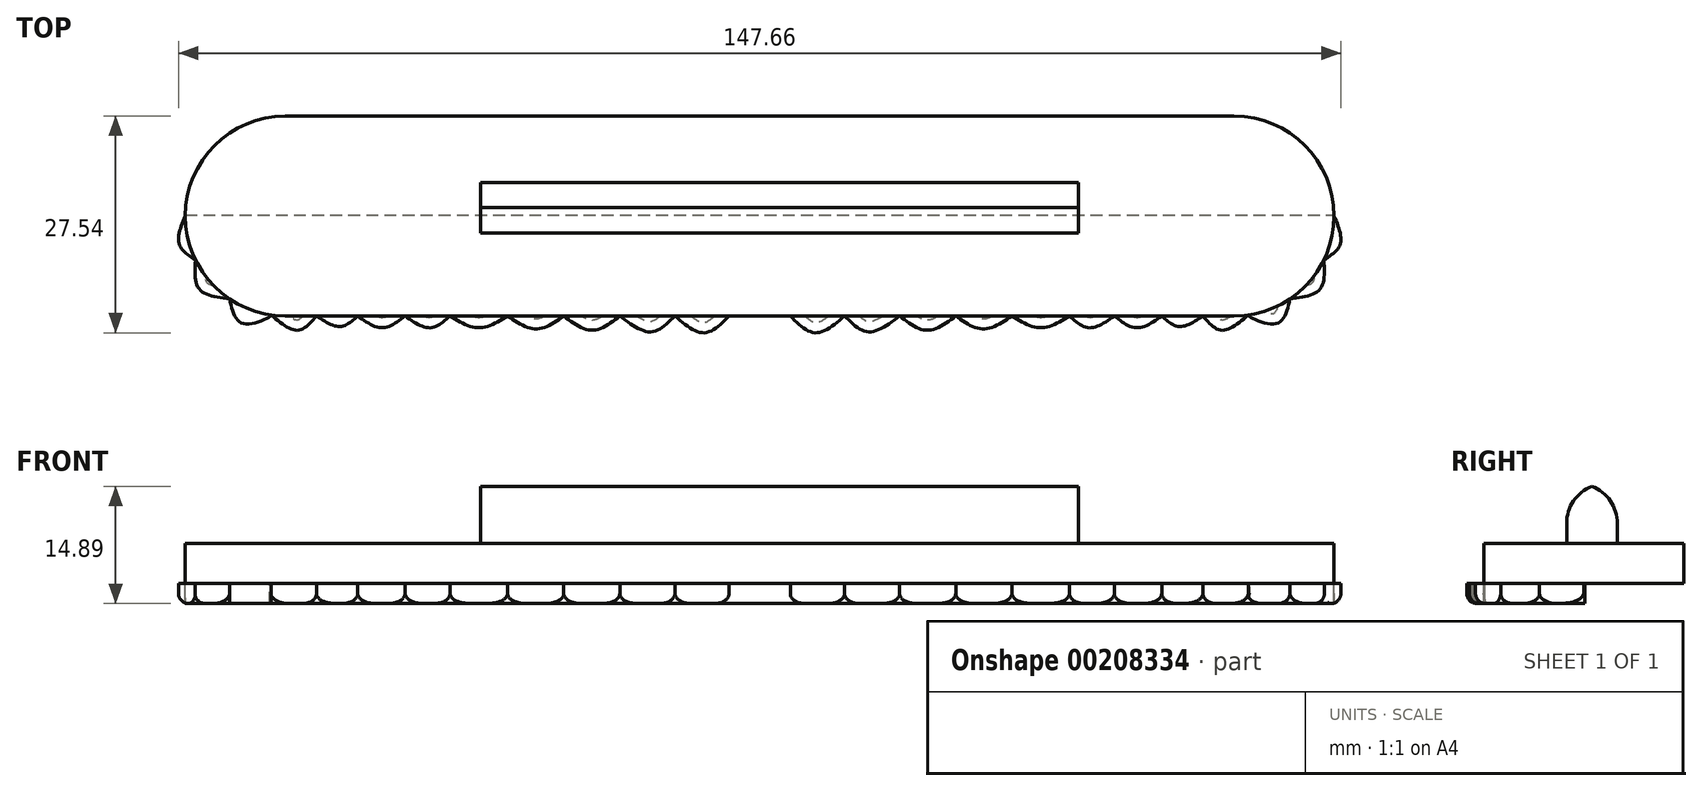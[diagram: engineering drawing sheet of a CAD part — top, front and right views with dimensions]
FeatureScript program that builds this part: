
annotation { "Feature Type Name" : "Feature", "Feature Type Description" : "" }
export const myFeature = defineFeature(function(context is Context, id is Id, definition is map)
    precondition{}
    {
        {
            var Q0;
            Q0=qCreatedBy(makeId("Top.planeOp"),FACE);
            var sketch = newSketch(context, id + "F0", { "sketchPlane" : qUnion([Q0])});
            skLineSegment(sketch, "E0.bottom", {"start": v(-28.22, 12.55) * mm, "end": v(92.3, 12.55) * mm});
            skLineSegment(sketch, "E0.top", {"start": v(-28.22, -12.85) * mm, "end": v(92.3, -12.85) * mm});
            skLineSegment(sketch, "E0.left", {"start": v(-28.22, 12.55) * mm, "end": v(-28.22, -12.85) * mm});
            skLineSegment(sketch, "E0.right", {"start": v(92.3, 12.55) * mm, "end": v(92.3, -12.85) * mm});
            skArc(sketch, "E1", {"start": v(-28.22, 12.55) * mm, "mid": v(-40.92, -0.15) * mm, "end": v(-28.22, -12.85) * mm});
            skArc(sketch, "E2", {"start": v(92.3, -12.85) * mm, "mid": v(105, -0.15) * mm, "end": v(92.3, 12.55) * mm});
            skSolve(sketch);
        }
        {
            var Q0;
            Q0=makeQuery(id+"F0.imprint","IMPRINT",FACE,{"disambiguationData":[TD([[makeQuery(id+"F0.imprint","IMPRINT",EDGE,{"derivedFrom":sQuery(id+"F0.wireOp",EDGE,"E0.left")}),-1.0]])]});
            var Q1;
            Q1=makeQuery(id+"F0.imprint","IMPRINT",FACE,{"disambiguationData":[TD([[makeQuery(id+"F0.imprint","IMPRINT",EDGE,{"derivedFrom":sQuery(id+"F0.wireOp",EDGE,"E0.bottom")}),-1.0]])]});
            var Q2;
            Q2=makeQuery(id+"F0.imprint","IMPRINT",FACE,{"disambiguationData":[TD([[makeQuery(id+"F0.imprint","IMPRINT",EDGE,{"derivedFrom":sQuery(id+"F0.wireOp",EDGE,"E0.right")}),1.0]])]});
            extrude(context, id + "F1", {"entities" : qUnion([Q0, Q1, Q2]), "depth" : 5.08 * mm});
        }
        {
            var Q0;
            Q0=makeQuery(id+"F1.opExtrude","CAP_FACE",FACE,{"disambiguationData":[OSD([sQuery(id+"F0.wireOp",EDGE,"E0.bottom"),sQuery(id+"F0.wireOp",EDGE,"E0.top"),sQuery(id+"F0.wireOp",EDGE,"E1"),sQuery(id+"F0.wireOp",EDGE,"E2")])],"isStart":true});
            var sketch = newSketch(context, id + "F2", { "sketchPlane" : qUnion([Q0])});
            skFitSpline(sketch, "E3", {"points": [v(-35.3, 10.7) * mm, v(-33.3, 13.87) * mm, v(-30.02, 12.73) * mm, v(-30.24, 12.7) * mm, v(-30.21, 12.7) * mm], "startDerivative": vector(2.37, 10.41) * mm, "endDerivative": vector(1.4, 0.2) * mm});
            skFitSpline(sketch, "E4", {"points": [v(-30.02, 12.73) * mm, v(-26.65, 14.67) * mm, v(-24.27, 12.85) * mm], "startDerivative": vector(6.67, 5.65) * mm, "endDerivative": vector(4.8, -5.64) * mm});
            skFitSpline(sketch, "E5", {"points": [v(-24.27, 12.85) * mm, v(-21.25, 14.2) * mm, v(-19.03, 12.85) * mm], "startDerivative": vector(5.94, 3.95) * mm, "endDerivative": vector(4.5, -4.1) * mm});
            skFitSpline(sketch, "E6", {"points": [v(-19.03, 12.85) * mm, v(-15.86, 14.35) * mm, v(-13, 12.85) * mm], "startDerivative": vector(6.31, 4.46) * mm, "endDerivative": vector(5.74, -4.52) * mm});
            skFitSpline(sketch, "E7", {"points": [v(-13, 12.85) * mm, v(-9.83, 14.35) * mm, v(-7.3, 12.85) * mm], "startDerivative": vector(6.28, 4.43) * mm, "endDerivative": vector(5.12, -4.56) * mm});
            skFitSpline(sketch, "E8", {"points": [v(-7.3, 12.85) * mm, v(-3.65, 14.35) * mm, v(0, 12.85) * mm], "startDerivative": vector(7.3, 4.49) * mm, "endDerivative": vector(7.3, -4.49) * mm});
            skFitSpline(sketch, "E9", {"points": [v(0, 12.85) * mm, v(3.65, 14.5) * mm, v(7.14, 12.85) * mm], "startDerivative": vector(7.28, 4.95) * mm, "endDerivative": vector(7, -4.98) * mm});
            skFitSpline(sketch, "E10", {"points": [v(7.14, 12.85) * mm, v(10.79, 14.67) * mm, v(14.27, 12.85) * mm], "startDerivative": vector(7.28, 5.42) * mm, "endDerivative": vector(7, -5.46) * mm});
            skLineSegment(sketch, "E11", {"start": v(32.04, 13.5) * mm, "end": v(32.04, 65.15) * mm});
            skPoint(sketch, "E11.startSnap0", {"position": v(32.04, 12.85) * mm});
            skLineSegment(sketch, "E12", {"start": v(32.04, 65.15) * mm, "end": v(32.04, -46.58) * mm});
            skPoint(sketch, "E12.endSnap0", {"position": v(32.04, -12.55) * mm});
            skLineSegment(sketch, "E13", {"start": v(-54.93, 0.15) * mm, "end": v(124.28, 0) * mm});
            skPoint(sketch, "E13.startSnap0", {"position": v(-40.92, 0.15) * mm});
            skFitSpline(sketch, "E14", {"points": [v(14.27, 12.85) * mm, v(18.2, 14.86) * mm, v(21.27, 12.85) * mm], "startDerivative": vector(7.77, 5.95) * mm, "endDerivative": vector(6.2, -6.13) * mm});
            skFitSpline(sketch, "E15", {"points": [v(21.27, 12.85) * mm, v(24.96, 14.99) * mm, v(28.15, 12.85) * mm], "startDerivative": vector(7.36, 6.35) * mm, "endDerivative": vector(6.41, -6.46) * mm});
            skFitSpline(sketch, "E16", {"points": [v(28.15, 12.85) * mm, v(32.04, 14.99) * mm, v(35.66, 12.85) * mm], "startDerivative": vector(7.75, 6.37) * mm, "endDerivative": vector(7.25, -6.43) * mm});
            skFitSpline(sketch, "E17", {"points": [v(-35.3, 10.7) * mm, v(-39.13, 9.45) * mm, v(-39.62, 5.76) * mm], "startDerivative": vector(-9.17, -1.14) * mm, "endDerivative": vector(0.62, -8.8) * mm});
            skFitSpline(sketch, "E18", {"points": [v(-39.62, 5.76) * mm, v(-41.72, 3.67) * mm, v(-40.92, 0.15) * mm], "startDerivative": vector(-5.81, -3.84) * mm, "endDerivative": vector(3.06, -7.3) * mm});
            skFitSpline(sketch, "E19.MirrorCS", {"points": [v(49.8, 12.85) * mm, v(45.89, 14.86) * mm, v(42.81, 12.85) * mm], "startDerivative": vector(-7.77, 5.95) * mm, "endDerivative": vector(-6.2, -6.13) * mm});
            skFitSpline(sketch, "E20.MirrorCS", {"points": [v(42.81, 12.85) * mm, v(39.12, 14.99) * mm, v(35.92, 12.85) * mm], "startDerivative": vector(-7.36, 6.35) * mm, "endDerivative": vector(-6.41, -6.46) * mm});
            skFitSpline(sketch, "E21.MirrorCS", {"points": [v(56.94, 12.85) * mm, v(53.3, 14.67) * mm, v(49.8, 12.85) * mm], "startDerivative": vector(-7.28, 5.42) * mm, "endDerivative": vector(-7, -5.46) * mm});
            skFitSpline(sketch, "E22.MirrorCS", {"points": [v(64.08, 12.85) * mm, v(60.43, 14.5) * mm, v(56.94, 12.85) * mm], "startDerivative": vector(-7.28, 4.95) * mm, "endDerivative": vector(-7, -4.98) * mm});
            skFitSpline(sketch, "E23.MirrorCS", {"points": [v(71.38, 12.85) * mm, v(67.73, 14.35) * mm, v(64.08, 12.85) * mm], "startDerivative": vector(-7.3, 4.49) * mm, "endDerivative": vector(-7.3, -4.49) * mm});
            skFitSpline(sketch, "E24.MirrorCS", {"points": [v(77.09, 12.85) * mm, v(73.91, 14.35) * mm, v(71.38, 12.85) * mm], "startDerivative": vector(-6.28, 4.43) * mm, "endDerivative": vector(-5.12, -4.56) * mm});
            skFitSpline(sketch, "E25.MirrorCS", {"points": [v(83.11, 12.85) * mm, v(79.94, 14.35) * mm, v(77.09, 12.85) * mm], "startDerivative": vector(-6.31, 4.46) * mm, "endDerivative": vector(-5.74, -4.52) * mm});
            skFitSpline(sketch, "E26.MirrorCS", {"points": [v(88.35, 12.85) * mm, v(85.33, 14.2) * mm, v(83.11, 12.85) * mm], "startDerivative": vector(-5.94, 3.95) * mm, "endDerivative": vector(-4.5, -4.1) * mm});
            skFitSpline(sketch, "E27.MirrorCS", {"points": [v(94.1, 12.73) * mm, v(90.73, 14.67) * mm, v(88.35, 12.85) * mm], "startDerivative": vector(-6.67, 5.65) * mm, "endDerivative": vector(-4.8, -5.64) * mm});
            skFitSpline(sketch, "E28.MirrorCS", {"points": [v(99.39, 10.7) * mm, v(97.39, 13.87) * mm, v(94.1, 12.73) * mm, v(94.32, 12.7) * mm, v(94.29, 12.7) * mm], "startDerivative": vector(-2.37, 10.41) * mm, "endDerivative": vector(-1.4, 0.2) * mm});
            skFitSpline(sketch, "E29.MirrorCS", {"points": [v(99.39, 10.7) * mm, v(103.21, 9.45) * mm, v(103.7, 5.76) * mm], "startDerivative": vector(9.17, -1.14) * mm, "endDerivative": vector(-0.62, -8.8) * mm});
            skFitSpline(sketch, "E30.MirrorCS", {"points": [v(103.7, 5.76) * mm, v(105.8, 3.67) * mm, v(105, 0.15) * mm], "startDerivative": vector(5.81, -3.84) * mm, "endDerivative": vector(-3.06, -7.3) * mm});
            skFitSpline(sketch, "E31.MirrorCS", {"points": [v(-39.63, -5.47) * mm, v(-41.72, -3.38) * mm, v(-40.92, 0.13) * mm], "startDerivative": vector(-5.8, 3.85) * mm, "endDerivative": vector(3.08, 7.3) * mm});
            skFitSpline(sketch, "E32.MirrorCS", {"points": [v(-35.33, -10.42) * mm, v(-39.15, -9.17) * mm, v(-39.63, -5.47) * mm], "startDerivative": vector(-9.17, 1.15) * mm, "endDerivative": vector(0.64, 8.8) * mm});
            skFitSpline(sketch, "E33.MirrorCS", {"points": [v(-35.33, -10.42) * mm, v(-33.33, -13.6) * mm, v(-30.05, -12.46) * mm, v(-30.27, -12.43) * mm, v(-30.23, -12.43) * mm], "startDerivative": vector(2.36, -10.41) * mm, "endDerivative": vector(1.4, -0.2) * mm});
            skFitSpline(sketch, "E34.MirrorCS", {"points": [v(-30.05, -12.46) * mm, v(-26.67, -14.4) * mm, v(-24.29, -12.6) * mm], "startDerivative": vector(6.66, -5.66) * mm, "endDerivative": vector(4.81, 5.63) * mm});
            skFitSpline(sketch, "E35.MirrorCS", {"points": [v(-24.29, -12.6) * mm, v(-21.28, -13.94) * mm, v(-19.06, -12.6) * mm], "startDerivative": vector(5.93, -3.96) * mm, "endDerivative": vector(4.5, 4.1) * mm});
            skFitSpline(sketch, "E36.MirrorCS", {"points": [v(-19.06, -12.6) * mm, v(-15.89, -14.1) * mm, v(-13.03, -12.62) * mm], "startDerivative": vector(6.3, -4.47) * mm, "endDerivative": vector(5.75, 4.51) * mm});
            skFitSpline(sketch, "E37.MirrorCS", {"points": [v(-13.03, -12.62) * mm, v(-9.86, -14.12) * mm, v(-7.32, -12.63) * mm], "startDerivative": vector(6.27, -4.44) * mm, "endDerivative": vector(5.13, 4.55) * mm});
            skFitSpline(sketch, "E38.MirrorCS", {"points": [v(-7.32, -12.63) * mm, v(-3.67, -14.13) * mm, v(-0.02, -12.64) * mm], "startDerivative": vector(7.29, -4.5) * mm, "endDerivative": vector(7.3, 4.47) * mm});
            skFitSpline(sketch, "E39.MirrorCS", {"points": [v(-0.02, -12.64) * mm, v(3.62, -14.3) * mm, v(7.12, -12.65) * mm], "startDerivative": vector(7.27, -4.96) * mm, "endDerivative": vector(7, 4.97) * mm});
            skFitSpline(sketch, "E40.MirrorCS", {"points": [v(7.12, -12.65) * mm, v(10.76, -14.47) * mm, v(14.25, -12.66) * mm], "startDerivative": vector(7.27, -5.44) * mm, "endDerivative": vector(7, 5.44) * mm});
            skFitSpline(sketch, "E41.MirrorCS", {"points": [v(14.25, -12.66) * mm, v(18.16, -14.68) * mm, v(21.24, -12.68) * mm], "startDerivative": vector(7.76, -5.96) * mm, "endDerivative": vector(6.2, 6.12) * mm});
            skFitSpline(sketch, "E42.MirrorCS", {"points": [v(14.25, -12.66) * mm, v(18.16, -14.68) * mm, v(21.24, -12.68) * mm], "startDerivative": vector(7.76, -5.96) * mm, "endDerivative": vector(6.2, 6.12) * mm});
            skFitSpline(sketch, "E43.MirrorCS", {"points": [v(21.24, -12.68) * mm, v(24.93, -14.82) * mm, v(28.13, -12.69) * mm], "startDerivative": vector(7.35, -6.36) * mm, "endDerivative": vector(6.42, 6.45) * mm});
            skFitSpline(sketch, "E44.MirrorCS", {"points": [v(28.13, -12.69) * mm, v(32.01, -14.83) * mm, v(35.64, -12.7) * mm], "startDerivative": vector(7.74, -6.38) * mm, "endDerivative": vector(7.26, 6.42) * mm});
            skFitSpline(sketch, "E45.MirrorCS", {"points": [v(42.8, -12.71) * mm, v(39.1, -14.84) * mm, v(35.9, -12.7) * mm], "startDerivative": vector(-7.37, -6.34) * mm, "endDerivative": vector(-6.4, 6.47) * mm});
            skFitSpline(sketch, "E46.MirrorCS", {"points": [v(49.78, -12.73) * mm, v(45.86, -14.73) * mm, v(42.8, -12.71) * mm], "startDerivative": vector(-7.78, -5.94) * mm, "endDerivative": vector(-6.18, 6.14) * mm});
            skFitSpline(sketch, "E47.MirrorCS", {"points": [v(56.92, -12.74) * mm, v(53.27, -14.55) * mm, v(49.78, -12.73) * mm], "startDerivative": vector(-7.29, -5.41) * mm, "endDerivative": vector(-6.98, 5.47) * mm});
            skFitSpline(sketch, "E48.MirrorCS", {"points": [v(64.06, -12.75) * mm, v(60.4, -14.4) * mm, v(56.92, -12.74) * mm], "startDerivative": vector(-7.29, -4.94) * mm, "endDerivative": vector(-6.99, 5) * mm});
            skFitSpline(sketch, "E49.MirrorCS", {"points": [v(77.06, -12.77) * mm, v(73.89, -14.26) * mm, v(71.35, -12.76) * mm], "startDerivative": vector(-6.29, -4.42) * mm, "endDerivative": vector(-5.11, 4.57) * mm});
            skFitSpline(sketch, "E50.MirrorCS", {"points": [v(77.06, -12.77) * mm, v(73.89, -14.26) * mm, v(71.35, -12.76) * mm], "startDerivative": vector(-6.29, -4.42) * mm, "endDerivative": vector(-5.11, 4.57) * mm});
            skFitSpline(sketch, "E51.MirrorCS", {"points": [v(77.06, -12.77) * mm, v(73.89, -14.26) * mm, v(71.35, -12.76) * mm], "startDerivative": vector(-6.29, -4.42) * mm, "endDerivative": vector(-5.11, 4.57) * mm});
            skFitSpline(sketch, "E52.MirrorCS", {"points": [v(71.35, -12.76) * mm, v(67.7, -14.25) * mm, v(64.06, -12.75) * mm], "startDerivative": vector(-7.3, -4.47) * mm, "endDerivative": vector(-7.29, 4.5) * mm});
            skFitSpline(sketch, "E53.MirrorCS", {"points": [v(83.1, -12.78) * mm, v(79.92, -14.27) * mm, v(77.06, -12.77) * mm], "startDerivative": vector(-6.32, -4.45) * mm, "endDerivative": vector(-5.73, 4.53) * mm});
            skFitSpline(sketch, "E54.MirrorCS", {"points": [v(88.32, -12.8) * mm, v(85.3, -14.12) * mm, v(83.1, -12.78) * mm], "startDerivative": vector(-5.95, -3.94) * mm, "endDerivative": vector(-4.5, 4.11) * mm});
            skFitSpline(sketch, "E55.MirrorCS", {"points": [v(94.08, -12.67) * mm, v(90.7, -14.6) * mm, v(88.32, -12.8) * mm], "startDerivative": vector(-6.68, -5.64) * mm, "endDerivative": vector(-4.8, 5.65) * mm});
            skFitSpline(sketch, "E56.MirrorCS", {"points": [v(99.37, -10.65) * mm, v(97.36, -13.83) * mm, v(94.08, -12.67) * mm, v(94.3, -12.64) * mm, v(94.27, -12.65) * mm], "startDerivative": vector(-2.4, -10.4) * mm, "endDerivative": vector(-1.4, -0.2) * mm});
            skFitSpline(sketch, "E57.MirrorCS", {"points": [v(103.69, -5.72) * mm, v(105.79, -3.64) * mm, v(105, -0.12) * mm], "startDerivative": vector(5.82, 3.83) * mm, "endDerivative": vector(-3.05, 7.31) * mm});
            skFitSpline(sketch, "E58.MirrorCS", {"points": [v(99.37, -10.65) * mm, v(103.2, -9.42) * mm, v(103.69, -5.72) * mm], "startDerivative": vector(9.17, 1.12) * mm, "endDerivative": vector(-0.6, 8.8) * mm});
            skSolve(sketch);
        }
        {
            var Q0;
            {var subQ0=sQuery(id+"F2.wireOp",EDGE,"E7");Q0=makeQuery(id+"F2.imprint","IMPRINT",FACE,{"disambiguationData":[TD([[makeQuery(id+"F2.imprint","IMPRINT",EDGE,{"derivedFrom":subQ0}),-1.0]])]});}
            var Q1;
            {var subQ0=sQuery(id+"F2.wireOp",EDGE,"E8");Q1=makeQuery(id+"F2.imprint","IMPRINT",FACE,{"disambiguationData":[TD([[makeQuery(id+"F2.imprint","IMPRINT",EDGE,{"derivedFrom":subQ0}),-1.0]])]});}
            var Q2;
            {var subQ0=sQuery(id+"F2.wireOp",EDGE,"E6");Q2=makeQuery(id+"F2.imprint","IMPRINT",FACE,{"disambiguationData":[TD([[makeQuery(id+"F2.imprint","IMPRINT",EDGE,{"derivedFrom":subQ0}),-1.0]])]});}
            var Q3;
            {var subQ0=sQuery(id+"F2.wireOp",EDGE,"E5");Q3=makeQuery(id+"F2.imprint","IMPRINT",FACE,{"disambiguationData":[TD([[makeQuery(id+"F2.imprint","IMPRINT",EDGE,{"derivedFrom":subQ0}),-1.0]])]});}
            var Q4;
            {var subQ0=sQuery(id+"F2.wireOp",EDGE,"E4");Q4=makeQuery(id+"F2.imprint","IMPRINT",FACE,{"disambiguationData":[TD([[makeQuery(id+"F2.imprint","IMPRINT",EDGE,{"derivedFrom":subQ0}),-1.0]])]});}
            var Q5;
            {var subQ0=sQuery(id+"F2.wireOp",EDGE,"E9");Q5=makeQuery(id+"F2.imprint","IMPRINT",FACE,{"disambiguationData":[TD([[makeQuery(id+"F2.imprint","IMPRINT",EDGE,{"derivedFrom":subQ0}),-1.0]])]});}
            var Q6;
            {var subQ0=sQuery(id+"F2.wireOp",EDGE,"E10");Q6=makeQuery(id+"F2.imprint","IMPRINT",FACE,{"disambiguationData":[TD([[makeQuery(id+"F2.imprint","IMPRINT",EDGE,{"derivedFrom":subQ0}),-1.0]])]});}
            var Q7;
            {var subQ0=sQuery(id+"F2.wireOp",EDGE,"E14");Q7=makeQuery(id+"F2.imprint","IMPRINT",FACE,{"disambiguationData":[TD([[makeQuery(id+"F2.imprint","IMPRINT",EDGE,{"derivedFrom":subQ0}),-1.0]])]});}
            var Q8;
            {var subQ0=sQuery(id+"F2.wireOp",EDGE,"E15");Q8=makeQuery(id+"F2.imprint","IMPRINT",FACE,{"disambiguationData":[TD([[makeQuery(id+"F2.imprint","IMPRINT",EDGE,{"derivedFrom":subQ0}),-1.0]])]});}
            var Q9;
            {var subQ0=sQuery(id+"F2.wireOp",EDGE,"E12");var subQ1=makeQuery(id+"F2.imprint","IMPRINT",VERTEX,{"derivedFrom":subQ0});Q9=makeQuery(id+"F2.imprint","IMPRINT",FACE,{"disambiguationData":[TD([[makeQuery(id+"F2.imprint","IMPRINT",EDGE,{"disambiguationData":[TD([[subQ1,1.0]])],"derivedFrom":subQ0}),-1.0]])]});}
            var Q10;
            {var subQ0=sQuery(id+"F2.wireOp",EDGE,"E12");var subQ1=makeQuery(id+"F2.imprint","IMPRINT",VERTEX,{"derivedFrom":subQ0});Q10=makeQuery(id+"F2.imprint","IMPRINT",FACE,{"disambiguationData":[TD([[makeQuery(id+"F2.imprint","IMPRINT",EDGE,{"disambiguationData":[TD([[subQ1,1.0]])],"derivedFrom":subQ0}),1.0]])]});}
            var Q11;
            {var subQ0=sQuery(id+"F2.wireOp",EDGE,"E20.MirrorCS");Q11=makeQuery(id+"F2.imprint","IMPRINT",FACE,{"disambiguationData":[TD([[makeQuery(id+"F2.imprint","IMPRINT",EDGE,{"derivedFrom":subQ0}),1.0]])]});}
            var Q12;
            {var subQ0=sQuery(id+"F2.wireOp",EDGE,"E19.MirrorCS");Q12=makeQuery(id+"F2.imprint","IMPRINT",FACE,{"disambiguationData":[TD([[makeQuery(id+"F2.imprint","IMPRINT",EDGE,{"derivedFrom":subQ0}),1.0]])]});}
            var Q13;
            {var subQ0=sQuery(id+"F2.wireOp",EDGE,"E21.MirrorCS");Q13=makeQuery(id+"F2.imprint","IMPRINT",FACE,{"disambiguationData":[TD([[makeQuery(id+"F2.imprint","IMPRINT",EDGE,{"derivedFrom":subQ0}),1.0]])]});}
            var Q14;
            {var subQ0=sQuery(id+"F2.wireOp",EDGE,"E22.MirrorCS");Q14=makeQuery(id+"F2.imprint","IMPRINT",FACE,{"disambiguationData":[TD([[makeQuery(id+"F2.imprint","IMPRINT",EDGE,{"derivedFrom":subQ0}),1.0]])]});}
            var Q15;
            {var subQ0=sQuery(id+"F2.wireOp",EDGE,"E23.MirrorCS");Q15=makeQuery(id+"F2.imprint","IMPRINT",FACE,{"disambiguationData":[TD([[makeQuery(id+"F2.imprint","IMPRINT",EDGE,{"derivedFrom":subQ0}),1.0]])]});}
            var Q16;
            {var subQ0=sQuery(id+"F2.wireOp",EDGE,"E24.MirrorCS");Q16=makeQuery(id+"F2.imprint","IMPRINT",FACE,{"disambiguationData":[TD([[makeQuery(id+"F2.imprint","IMPRINT",EDGE,{"derivedFrom":subQ0}),1.0]])]});}
            var Q17;
            {var subQ0=sQuery(id+"F2.wireOp",EDGE,"E25.MirrorCS");Q17=makeQuery(id+"F2.imprint","IMPRINT",FACE,{"disambiguationData":[TD([[makeQuery(id+"F2.imprint","IMPRINT",EDGE,{"derivedFrom":subQ0}),1.0]])]});}
            var Q18;
            {var subQ0=sQuery(id+"F2.wireOp",EDGE,"E26.MirrorCS");Q18=makeQuery(id+"F2.imprint","IMPRINT",FACE,{"disambiguationData":[TD([[makeQuery(id+"F2.imprint","IMPRINT",EDGE,{"derivedFrom":subQ0}),1.0]])]});}
            var Q19;
            {var subQ0=sQuery(id+"F2.wireOp",EDGE,"E27.MirrorCS");Q19=makeQuery(id+"F2.imprint","IMPRINT",FACE,{"disambiguationData":[TD([[makeQuery(id+"F2.imprint","IMPRINT",EDGE,{"derivedFrom":subQ0}),1.0]])]});}
            var Q20;
            {var subQ0=sQuery(id+"F2.wireOp",EDGE,"E28.MirrorCS");var subQ1=makeQuery(id+"F1.opExtrude","CAP_EDGE",EDGE,{"disambiguationData":[OSD([sQuery(id+"F0.wireOp",EDGE,"E2")])],"isStart":true});var subQ4=makeQuery(id+"F2.imprint","INTERSECT",VERTEX,{"disambiguationData":[OD(0.0)],"derivedFrom":[subQ1,subQ0]});Q20=makeQuery(id+"F2.imprint","IMPRINT",FACE,{"disambiguationData":[TD([[makeQuery(id+"F2.imprint","IMPRINT",EDGE,{"disambiguationData":[TD([[subQ4,1.0]])],"derivedFrom":subQ0}),-1.0]])]});}
            var Q21;
            {var subQ0=sQuery(id+"F2.wireOp",EDGE,"E29.MirrorCS");Q21=makeQuery(id+"F2.imprint","IMPRINT",FACE,{"disambiguationData":[TD([[makeQuery(id+"F2.imprint","IMPRINT",EDGE,{"derivedFrom":subQ0}),-1.0]])]});}
            var Q22;
            {var subQ0=sQuery(id+"F2.wireOp",EDGE,"E30.MirrorCS");Q22=makeQuery(id+"F2.imprint","IMPRINT",FACE,{"disambiguationData":[TD([[makeQuery(id+"F2.imprint","IMPRINT",EDGE,{"derivedFrom":subQ0}),-1.0]])]});}
            var Q23;
            {var subQ0=sQuery(id+"F2.wireOp",EDGE,"E17");Q23=makeQuery(id+"F2.imprint","IMPRINT",FACE,{"disambiguationData":[TD([[makeQuery(id+"F2.imprint","IMPRINT",EDGE,{"derivedFrom":subQ0}),1.0]])]});}
            var Q24;
            {var subQ0=sQuery(id+"F2.wireOp",EDGE,"E18");Q24=makeQuery(id+"F2.imprint","IMPRINT",FACE,{"disambiguationData":[TD([[makeQuery(id+"F2.imprint","IMPRINT",EDGE,{"derivedFrom":subQ0}),1.0]])]});}
            var Q25;
            {var subQ0=sQuery(id+"F2.wireOp",EDGE,"E3");var subQ1=makeQuery(id+"F1.opExtrude","CAP_EDGE",EDGE,{"disambiguationData":[OSD([sQuery(id+"F0.wireOp",EDGE,"E1")])],"isStart":true});var subQ4=makeQuery(id+"F2.imprint","INTERSECT",VERTEX,{"disambiguationData":[OD(0.0)],"derivedFrom":[subQ1,subQ0]});Q25=makeQuery(id+"F2.imprint","IMPRINT",FACE,{"disambiguationData":[TD([[makeQuery(id+"F2.imprint","IMPRINT",EDGE,{"disambiguationData":[TD([[subQ4,1.0]])],"derivedFrom":subQ0}),1.0]])]});}
            extrude(context, id + "F3", {"entities" : qUnion([Q0, Q1, Q2, Q3, Q4, Q5, Q6, Q7, Q8, Q9, Q10, Q11, Q12, Q13, Q14, Q15, Q16, Q17, Q18, Q19, Q20, Q21, Q22, Q23, Q24, Q25]), "depth" : 2.54 * mm});
        }
        {
            var Q0;
            Q0=makeQuery(id+"F1.opExtrude","CAP_FACE",FACE,{"disambiguationData":[OSD([sQuery(id+"F0.wireOp",EDGE,"E0.bottom"),sQuery(id+"F0.wireOp",EDGE,"E0.top"),sQuery(id+"F0.wireOp",EDGE,"E1"),sQuery(id+"F0.wireOp",EDGE,"E2")])],"isStart":true});
            var sketch = newSketch(context, id + "F4", { "sketchPlane" : qUnion([Q0])});
            skLineSegment(sketch, "E59", {"start": v(-40.92, 0) * mm, "end": v(105, 0) * mm});
            skLineSegment(sketch, "E60", {"start": v(-28.22, 12.85) * mm, "end": v(92.3, 12.85) * mm});
            skArc(sketch, "E61", {"start": v(-28.22, 12.85) * mm, "mid": v(-37.26, 9.08) * mm, "end": v(-40.92, 0) * mm});
            skArc(sketch, "E62", {"start": v(105, 0) * mm, "mid": v(101.34, 9.08) * mm, "end": v(92.3, 12.85) * mm});
            skSolve(sketch);
        }
        {
            var Q0;
            Q0=makeQuery(id+"F4.imprint","IMPRINT",FACE,{"disambiguationData":[TD([[makeQuery(id+"F4.imprint","IMPRINT",EDGE,{"derivedFrom":sQuery(id+"F4.wireOp",EDGE,"E59")}),1.0]])]});
            extrude(context, id + "F5", {"entities" : qUnion([Q0]), "depth" : 2.54 * mm});
        }
        {
            var Q0;
            Q0=makeQuery(id+"F1.opExtrude","CAP_FACE",FACE,{"disambiguationData":[OSD([sQuery(id+"F0.wireOp",EDGE,"E0.bottom"),sQuery(id+"F0.wireOp",EDGE,"E0.top"),sQuery(id+"F0.wireOp",EDGE,"E1"),sQuery(id+"F0.wireOp",EDGE,"E2")])],"isStart":false});
            var sketch = newSketch(context, id + "F6", { "sketchPlane" : qUnion([Q0])});
            skLineSegment(sketch, "E63.bottom", {"start": v(-3.44, 4.12) * mm, "end": v(72.51, 4.12) * mm});
            skLineSegment(sketch, "E63.top", {"start": v(-3.44, -2.32) * mm, "end": v(72.51, -2.32) * mm});
            skLineSegment(sketch, "E63.left", {"start": v(-3.44, 4.12) * mm, "end": v(-3.44, -2.32) * mm});
            skLineSegment(sketch, "E63.right", {"start": v(72.51, 4.12) * mm, "end": v(72.51, -2.32) * mm});
            skSolve(sketch);
        }
        {
            var Q0;
            Q0=makeQuery(id+"F6.imprint","IMPRINT",FACE,{"disambiguationData":[TD([[makeQuery(id+"F6.imprint","IMPRINT",EDGE,{"derivedFrom":sQuery(id+"F6.wireOp",EDGE,"E63.bottom")}),-1.0]])]});
            extrude(context, id + "F7", {"entities" : qUnion([Q0]), "operationType" : NewBodyOperationType.ADD, "depth" : 7.62 * mm});
        }
        {
            var Q0;
            Q0=makeQuery(id+"F7.opExtrude","CAP_EDGE",EDGE,{"disambiguationData":[OSD([sQuery(id+"F6.wireOp",EDGE,"E63.top")])],"isStart":false});
            var Q1;
            Q1=makeQuery(id+"F7.opExtrude","CAP_EDGE",EDGE,{"disambiguationData":[OSD([sQuery(id+"F6.wireOp",EDGE,"E63.bottom")])],"isStart":false});
            fillet(context, id + "F8", {"entities" : qUnion([Q0, Q1]), "radius" : 5.08 * mm, "tangentPropagation" : true, "allowEdgeOverflow" : false});
        }
        {
            var Q0;
            Q0=makeQuery(id+"F3.opExtrude","CAP_EDGE",EDGE,{"disambiguationData":[OSD([sQuery(id+"F2.wireOp",EDGE,"E5")])],"isStart":false});
            var Q1;
            Q1=makeQuery(id+"F3.opExtrude","CAP_EDGE",EDGE,{"disambiguationData":[OSD([sQuery(id+"F2.wireOp",EDGE,"E6")])],"isStart":false});
            var Q2;
            Q2=makeQuery(id+"F3.opExtrude","CAP_EDGE",EDGE,{"disambiguationData":[OSD([sQuery(id+"F2.wireOp",EDGE,"E7")])],"isStart":false});
            var Q3;
            Q3=makeQuery(id+"F3.opExtrude","CAP_EDGE",EDGE,{"disambiguationData":[OSD([sQuery(id+"F2.wireOp",EDGE,"E8")])],"isStart":false});
            var Q4;
            Q4=makeQuery(id+"F3.opExtrude","CAP_EDGE",EDGE,{"disambiguationData":[OSD([sQuery(id+"F2.wireOp",EDGE,"E9")])],"isStart":false});
            var Q5;
            Q5=makeQuery(id+"F3.opExtrude","CAP_EDGE",EDGE,{"disambiguationData":[OSD([sQuery(id+"F2.wireOp",EDGE,"E10")])],"isStart":false});
            var Q6;
            Q6=makeQuery(id+"F3.opExtrude","CAP_EDGE",EDGE,{"disambiguationData":[OSD([sQuery(id+"F2.wireOp",EDGE,"E14")])],"isStart":false});
            var Q7;
            Q7=makeQuery(id+"F3.opExtrude","CAP_EDGE",EDGE,{"disambiguationData":[OSD([sQuery(id+"F2.wireOp",EDGE,"E15")])],"isStart":false});
            var Q8;
            Q8=makeQuery(id+"F3.opExtrude","CAP_EDGE",EDGE,{"disambiguationData":[OSD([sQuery(id+"F2.wireOp",EDGE,"E16")])],"isStart":false});
            var Q9;
            Q9=makeQuery(id+"F3.opExtrude","CAP_EDGE",EDGE,{"disambiguationData":[OSD([sQuery(id+"F2.wireOp",EDGE,"E20.MirrorCS")])],"isStart":false});
            var Q10;
            Q10=makeQuery(id+"F3.opExtrude","CAP_EDGE",EDGE,{"disambiguationData":[OSD([sQuery(id+"F2.wireOp",EDGE,"E19.MirrorCS")])],"isStart":false});
            var Q11;
            Q11=makeQuery(id+"F3.opExtrude","CAP_EDGE",EDGE,{"disambiguationData":[OSD([sQuery(id+"F2.wireOp",EDGE,"E21.MirrorCS")])],"isStart":false});
            var Q12;
            Q12=makeQuery(id+"F3.opExtrude","CAP_EDGE",EDGE,{"disambiguationData":[OSD([sQuery(id+"F2.wireOp",EDGE,"E22.MirrorCS")])],"isStart":false});
            var Q13;
            Q13=makeQuery(id+"F3.opExtrude","CAP_EDGE",EDGE,{"disambiguationData":[OSD([sQuery(id+"F2.wireOp",EDGE,"E17")])],"isStart":false});
            var Q14;
            {var subQ0=sQuery(id+"F2.wireOp",EDGE,"E3");var subQ1=makeQuery(id+"F1.opExtrude","CAP_EDGE",EDGE,{"disambiguationData":[OSD([sQuery(id+"F0.wireOp",EDGE,"E1")])],"isStart":true});Q14=makeQuery(id+"F3.opExtrude","CAP_EDGE",EDGE,{"disambiguationData":[OSD([subQ0]),TDD([makeQuery(id+"F2.imprint","IMPRINT",EDGE,{"disambiguationData":[TD([[makeQuery(id+"F2.imprint","INTERSECT",VERTEX,{"derivedFrom":[subQ1,subQ0,sQuery(id+"F2.wireOp",EDGE,"E17")]}),-1.0]])],"derivedFrom":subQ0})])],"isStart":false});}
            var Q15;
            Q15=makeQuery(id+"F3.opExtrude","CAP_EDGE",EDGE,{"disambiguationData":[OSD([sQuery(id+"F2.wireOp",EDGE,"E4")])],"isStart":false});
            var Q16;
            Q16=makeQuery(id+"F3.opExtrude","CAP_EDGE",EDGE,{"disambiguationData":[OSD([sQuery(id+"F2.wireOp",EDGE,"E18")])],"isStart":false});
            var Q17;
            Q17=makeQuery(id+"F3.opExtrude","CAP_EDGE",EDGE,{"disambiguationData":[OSD([sQuery(id+"F2.wireOp",EDGE,"E23.MirrorCS")])],"isStart":false});
            var Q18;
            Q18=makeQuery(id+"F3.opExtrude","CAP_EDGE",EDGE,{"disambiguationData":[OSD([sQuery(id+"F2.wireOp",EDGE,"E24.MirrorCS")])],"isStart":false});
            var Q19;
            Q19=makeQuery(id+"F3.opExtrude","CAP_EDGE",EDGE,{"disambiguationData":[OSD([sQuery(id+"F2.wireOp",EDGE,"E25.MirrorCS")])],"isStart":false});
            var Q20;
            Q20=makeQuery(id+"F3.opExtrude","CAP_EDGE",EDGE,{"disambiguationData":[OSD([sQuery(id+"F2.wireOp",EDGE,"E26.MirrorCS")])],"isStart":false});
            var Q21;
            Q21=makeQuery(id+"F3.opExtrude","CAP_EDGE",EDGE,{"disambiguationData":[OSD([sQuery(id+"F2.wireOp",EDGE,"E27.MirrorCS")])],"isStart":false});
            var Q22;
            {var subQ0=sQuery(id+"F2.wireOp",EDGE,"E28.MirrorCS");var subQ1=makeQuery(id+"F1.opExtrude","CAP_EDGE",EDGE,{"disambiguationData":[OSD([sQuery(id+"F0.wireOp",EDGE,"E2")])],"isStart":true});Q22=makeQuery(id+"F3.opExtrude","CAP_EDGE",EDGE,{"disambiguationData":[OSD([subQ0]),TDD([makeQuery(id+"F2.imprint","IMPRINT",EDGE,{"disambiguationData":[TD([[makeQuery(id+"F2.imprint","INTERSECT",VERTEX,{"derivedFrom":[subQ1,sQuery(id+"F2.wireOp",EDGE,"E27.MirrorCS"),subQ0]}),1.0]])],"derivedFrom":subQ0})])],"isStart":false});}
            var Q23;
            Q23=makeQuery(id+"F3.opExtrude","CAP_EDGE",EDGE,{"disambiguationData":[OSD([sQuery(id+"F2.wireOp",EDGE,"E29.MirrorCS")])],"isStart":false});
            var Q24;
            Q24=makeQuery(id+"F3.opExtrude","CAP_EDGE",EDGE,{"disambiguationData":[OSD([sQuery(id+"F2.wireOp",EDGE,"E30.MirrorCS")])],"isStart":false});
            fillet(context, id + "F9", {"entities" : qUnion([Q0, Q1, Q2, Q3, Q4, Q5, Q6, Q7, Q8, Q9, Q10, Q11, Q12, Q13, Q14, Q15, Q16, Q17, Q18, Q19, Q20, Q21, Q22, Q23, Q24]), "radius" : 1.27 * mm, "tangentPropagation" : true, "allowEdgeOverflow" : false});
        }
    });
